# Revit family: MKT3H-800(100,1200,1400)G70A
name_source: partatom
category: Mechanical Equipment
revit_build: Autodesk Revit 2013 (Build: 20120221_2030(x64)
units: mm (PartAtom-declared; Revit-internal decimal feet)

## types (4) — shared parameters
Condensation = water
Depth = 816 mm  [stored 2.67717 ft]
Description = High efficiency water cooled
Drain pipe = 32 mm
Height = 400 mm  [stored 1.31234 ft]
Installation = Indoor installation
Liquid pipe = 19.05 mm  [stored 0.0625 ft]
Manufacturer = Midea
Power supply = 220-240V ~50Hz
Rated current = 2 A
Series = FCU
Width = 946 mm  [stored 3.10367 ft]
clearance access behind = 200 mm  [stored 0.656168 ft]
clearance access left = 500 mm  [stored 1.64042 ft]
clearance access right = 500 mm  [stored 1.64042 ft]
zero-valued in all types: clearance access front

## per-type parameters (varying)
| type | Air Flow(H/M/L) | Cooling Capacity(H/M/L) | Heating Capacity(H/M/L) | Net Weight | Power Input(H/M/L) |
| MKT3H-800G70A | 1464/1453/1408 m3/h | 5.4/5.27/5.08 kW | 8.09/7.82/7.42 kW | 50.00 kg | 391/375/348 W |
| MKT3H-1000G70A | 1507/1491/1397 m3/h | 7.75/7.56/6.98 kW | 9.62/9.28/8.85 kW | 52.00 kg | 382/363/343 W |
| MKT3H-1200G70A | 1601/1557/1500 m3/h | 8.03/7.8/7.49 kW | 10.33/10.02/9.17 kW | 52.00 kg | 386/372/355 W |
| MKT3H-1400G70A | 1659/1590/1501 m3/h | 10.41/10.11/9.69 kW | 11.15/10.46/9.65 kW | 54.00 kg | 380/364/347 W |

note: column(s) folded — value = type name in every type: Model

note: [stored X ft] marks values corroborated as IEEE doubles in the binary element streams (Revit-internal decimal feet)

## geometry (parser evidence)
native form markers: Blend x2, Sweep x5
no freeform markers — native parametric forms only
